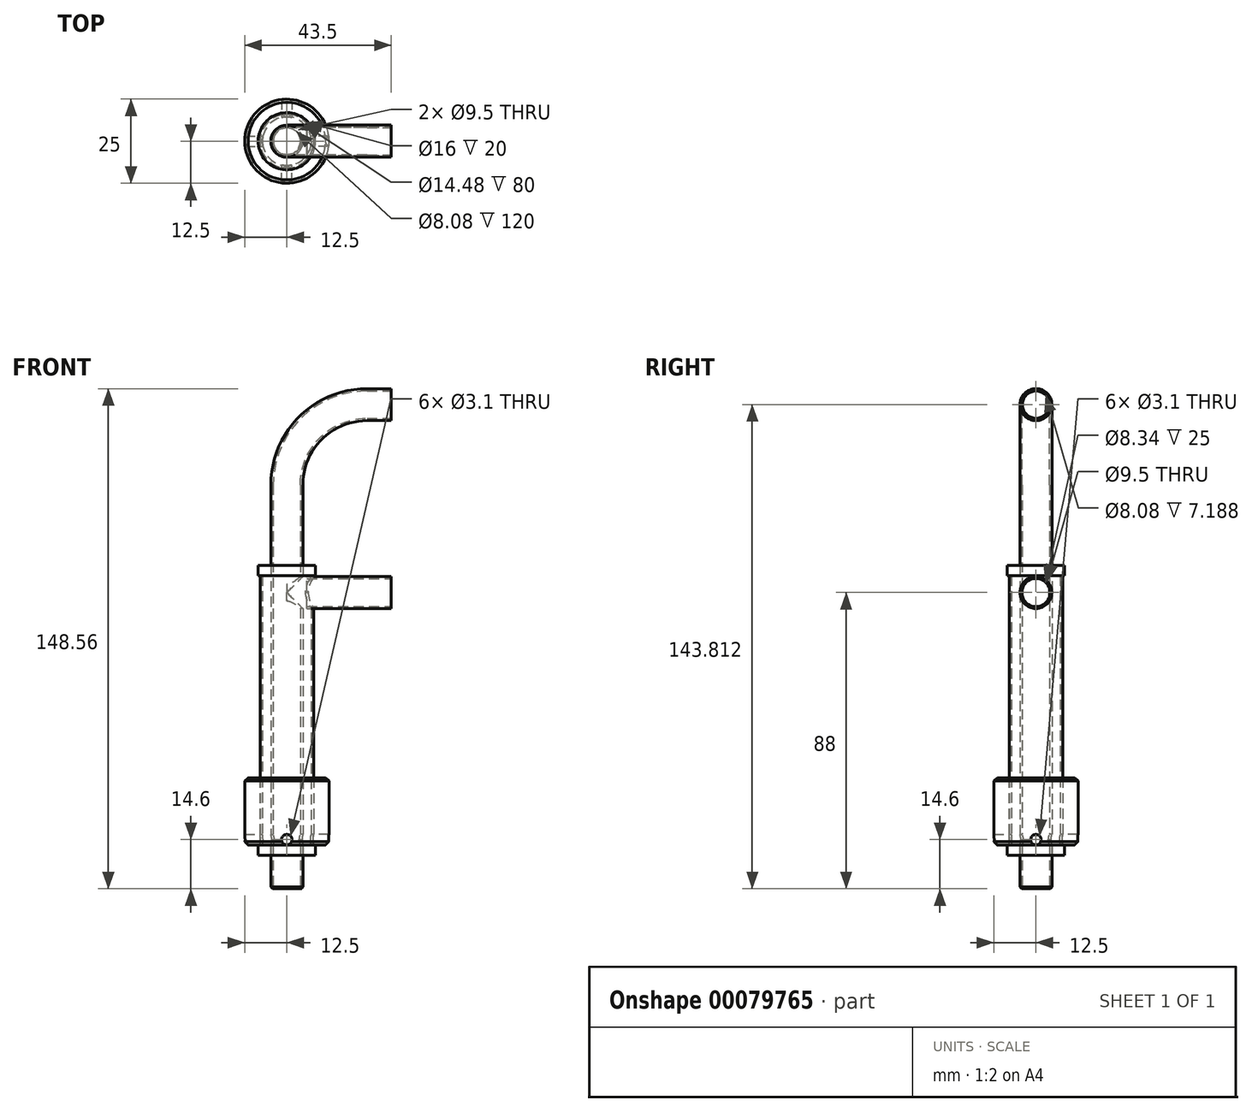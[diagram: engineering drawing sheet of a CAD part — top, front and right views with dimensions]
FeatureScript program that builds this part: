
annotation { "Feature Type Name" : "Feature", "Feature Type Description" : "" }
export const myFeature = defineFeature(function(context is Context, id is Id, definition is map)
    precondition{}
    {
        {
            var Q0;
            Q0=qCreatedBy(makeId("Top.planeOp"),FACE);
            var sketch = newSketch(context, id + "F0", { "sketchPlane" : qUnion([Q0])});
            skCircle(sketch, "E0", {"center": v(0, 0) * mm, "radius": 4.75 * mm});
            skCircle(sketch, "E1", {"center": v(0, 0) * mm, "radius": 4.04 * mm});
            skCircle(sketch, "E2", {"center": v(0, 0) * mm, "radius": 7.24 * mm});
            skCircle(sketch, "E3", {"center": v(0, 0) * mm, "radius": 7.95 * mm});
            skCircle(sketch, "E4", {"center": v(0, 0) * mm, "radius": 8.5 * mm});
            skSolve(sketch);
        }
        {
            var Q0;
            Q0=makeQuery(id+"F0.imprint","IMPRINT",FACE,{"disambiguationData":[TD([[makeQuery(id+"F0.imprint","IMPRINT",EDGE,{"derivedFrom":sQuery(id+"F0.wireOp",EDGE,"E0")}),1.0]])]});
            extrude(context, id + "F1", {"entities" : qUnion([Q0]), "depth" : 107 * mm, "hasSecondDirection" : true, "secondDirectionOppositeDirection" : true, "secondDirectionDepth" : 13 * mm});
        }
        {
            var Q0;
            Q0=makeQuery(id+"F0.imprint","IMPRINT",FACE,{"disambiguationData":[TD([[makeQuery(id+"F0.imprint","IMPRINT",EDGE,{"derivedFrom":sQuery(id+"F0.wireOp",EDGE,"E2")}),-1.0]])]});
            extrude(context, id + "F2", {"entities" : qUnion([Q0]), "depth" : 80 * mm});
        }
        {
            var Q0;
            Q0=makeQuery(id+"F0.imprint","IMPRINT",FACE,{"disambiguationData":[TD([[makeQuery(id+"F0.imprint","IMPRINT",EDGE,{"derivedFrom":sQuery(id+"F0.wireOp",EDGE,"E3")}),-1.0]])]});
            var Q1;
            Q1=makeQuery(id+"F0.imprint","IMPRINT",FACE,{"disambiguationData":[TD([[makeQuery(id+"F0.imprint","IMPRINT",EDGE,{"derivedFrom":sQuery(id+"F0.wireOp",EDGE,"E0")}),-1.0]])]});
            var Q2;
            Q2=makeQuery(id+"F0.imprint","IMPRINT",FACE,{"disambiguationData":[TD([[makeQuery(id+"F0.imprint","IMPRINT",EDGE,{"derivedFrom":sQuery(id+"F0.wireOp",EDGE,"E2")}),-1.0]])]});
            extrude(context, id + "F3", {"entities" : qUnion([Q0, Q1, Q2]), "oppositeDirection" : true, "depth" : 3 * mm});
        }
        {
            var Q0;
            Q0=qCreatedBy(makeId("Front.planeOp"),FACE);
            var sketch = newSketch(context, id + "F4", { "sketchPlane" : qUnion([Q0])});
            skLineSegment(sketch, "E5.bottom", {"start": v(8, 0) * mm, "end": v(12.5, 0) * mm});
            skLineSegment(sketch, "E5.top", {"start": v(8, 20) * mm, "end": v(12.5, 20) * mm});
            skLineSegment(sketch, "E5.left", {"start": v(8, 0) * mm, "end": v(8, 20) * mm});
            skLineSegment(sketch, "E5.right", {"start": v(12.5, 0) * mm, "end": v(12.5, 20) * mm});
            skLineSegment(sketch, "E6", {"start": v(0, 0) * mm, "end": v(0, 16.7) * mm, "construction": true});
            skSolve(sketch);
        }
        {
            var Q0;
            Q0=makeQuery(id+"F4.imprint","IMPRINT",FACE,{"disambiguationData":[TD([[makeQuery(id+"F4.imprint","IMPRINT",EDGE,{"derivedFrom":sQuery(id+"F4.wireOp",EDGE,"E5.bottom")}),1.0]])]});
            var Q1;
            Q1=sQuery(id+"F4.wireOp",EDGE,"E6");
            revolve(context, id + "F5", {"entities" : qUnion([Q0]), "axis" : qUnion([Q1]), "revolveType" : RevolveType.FULL});
        }
        {
            var Q0;
            Q0=qCreatedBy(makeId("Front.planeOp"),FACE);
            var sketch = newSketch(context, id + "F6", { "sketchPlane" : qUnion([Q0])});
            skCircle(sketch, "E7", {"center": v(0, 1.6) * mm, "radius": 1.55 * mm});
            skSolve(sketch);
        }
        {
            var Q0;
            Q0=qSketchRegion(id+"F6",true);
            extrude(context, id + "F7", {"entities" : qUnion([Q0]), "operationType" : NewBodyOperationType.REMOVE, "endBound" : BoundingType.THROUGH_ALL, "oppositeDirection" : true, "depth" : 25 * mm});
        }
        {
            var Q0;
            Q0=makeQuery(id+"F7.boolean.opBoolean","COPY",FACE,{"derivedFrom":makeQuery(id+"F7.opExtrude","SWEPT_FACE",FACE,{"disambiguationData":[OSD([sQuery(id+"F6.wireOp",EDGE,"E7")])]})});
            var Q1;
            Q1=makeQuery(id+"F2.opExtrude","SWEPT_FACE",FACE,{"disambiguationData":[OSD([sQuery(id+"F0.wireOp",EDGE,"E3")])]});
            circularPattern(context, id + "F8", {"faces" : qUnion([Q0]), "axis" : qUnion([Q1]), "angle" : 360 * degree, "instanceCount" : round(4), "equalSpace" : true, "patternType" : PatternType.FACE});
        }
        {
            var Q0;
            Q0=makeQuery(id+"F1.opExtrude","CAP_EDGE",EDGE,{"disambiguationData":[OSD([sQuery(id+"F0.wireOp",EDGE,"E0")])],"isStart":true});
            chamfer(context, id + "F9", {"entities" : qUnion([Q0]), "width" : 0.5 * mm, "tangentPropagation" : true});
        }
        {
            var Q0;
            Q0=makeQuery(id+"F2.opExtrude","CAP_FACE",FACE,{"disambiguationData":[OSD([sQuery(id+"F0.wireOp",EDGE,"E2"),sQuery(id+"F0.wireOp",EDGE,"E3")])],"isStart":false});
            var sketch = newSketch(context, id + "F10", { "sketchPlane" : qUnion([Q0])});
            skCircle(sketch, "E8", {"center": v(0, 0) * mm, "radius": 8.5 * mm});
            skCircle(sketch, "E9.0", {"center": v(0, 0) * mm, "radius": 4.75 * mm});
            skSolve(sketch);
        }
        {
            var Q0;
            Q0=qSketchRegion(id+"F10",true);
            extrude(context, id + "F11", {"entities" : qUnion([Q0]), "depth" : 3 * mm});
        }
        {
            var Q0;
            Q0=qCreatedBy(makeId("Right.planeOp"),FACE);
            var sketch = newSketch(context, id + "F12", { "sketchPlane" : qUnion([Q0])});
            skCircle(sketch, "E10", {"center": v(0, 75) * mm, "radius": 4.75 * mm});
            skSolve(sketch);
        }
        {
            var Q0;
            Q0=qSketchRegion(id+"F12",true);
            extrude(context, id + "F13", {"entities" : qUnion([Q0]), "operationType" : NewBodyOperationType.REMOVE, "endBound" : BoundingType.THROUGH_ALL, "depth" : 25 * mm});
        }
        {
            var Q0;
            Q0=qCreatedBy(makeId("Right.planeOp"),FACE);
            cPlane(context, id + "F14", {"entities" : qUnion([Q0]), "cplaneType" : CPlaneType.OFFSET, "offset" : 31 * mm, "width" : 150 * mm, "height" : 150 * mm});
        }
        {
            var Q0;
            Q0=qCreatedBy(id+"F14.planeOp",FACE);
            var sketch = newSketch(context, id + "F15", { "sketchPlane" : qUnion([Q0])});
            skCircle(sketch, "E11", {"center": v(0, 75) * mm, "radius": 4.17 * mm});
            skCircle(sketch, "E12", {"center": v(0, 75) * mm, "radius": 4.75 * mm});
            skSolve(sketch);
        }
        {
            var Q0;
            Q0=makeQuery(id+"F15.imprint","IMPRINT",FACE,{"disambiguationData":[TD([[makeQuery(id+"F15.imprint","IMPRINT",EDGE,{"derivedFrom":sQuery(id+"F15.wireOp",EDGE,"E11")}),-1.0]])]});
            var Q1;
            Q1=makeQuery(id+"F2.opExtrude","SWEPT_FACE",FACE,{"disambiguationData":[OSD([sQuery(id+"F0.wireOp",EDGE,"E2")])]});
            extrude(context, id + "F16", {"entities" : qUnion([Q0]), "oppositeDirection" : true, "endBoundEntityFace" : qUnion([Q1]), "depth" : 25 * mm});
        }
        {
            var Q0;
            Q0=qCreatedBy(makeId("Front.planeOp"),FACE);
            var sketch = newSketch(context, id + "F17", { "sketchPlane" : qUnion([Q0])});
            skPoint(sketch, "E13.0", {"position": v(31, 75) * mm});
            skArc(sketch, "E14", {"start": v(31, 75) * mm, "mid": v(41.08, 79.17) * mm, "end": v(45.25, 89.25) * mm});
            skLineSegment(sketch, "E15", {"start": v(45.25, 89.25) * mm, "end": v(45.25, 119.25) * mm});
            skSolve(sketch);
        }
        {
            var Q0;
            Q0=makeQuery(id+"F5.opRevolve","SWEPT_EDGE",EDGE,{"disambiguationData":[OSD([sQuery(id+"F4.wireOp",EDGE,"E5.bottom"),sQuery(id+"F4.wireOp",EDGE,"E5.right")])]});
            var Q1;
            Q1=makeQuery(id+"F5.opRevolve","SWEPT_EDGE",EDGE,{"disambiguationData":[OSD([sQuery(id+"F4.wireOp",EDGE,"E5.top"),sQuery(id+"F4.wireOp",EDGE,"E5.right")])]});
            chamfer(context, id + "F18", {"entities" : qUnion([Q0, Q1]), "width" : 1 * mm, "tangentPropagation" : true});
        }
        {
            var Q0;
            Q0=qCreatedBy(makeId("Front.planeOp"),FACE);
            var sketch = newSketch(context, id + "F19", { "sketchPlane" : qUnion([Q0])});
            skLineSegment(sketch, "E16.0", {"start": v(-4.04, 107) * mm, "end": v(4.04, 107) * mm, "construction": true});
            skLineSegment(sketch, "E17", {"start": v(23.81, 130.81) * mm, "end": v(31, 130.81) * mm});
            skArc(sketch, "E18", {"start": v(23.81, 130.81) * mm, "mid": v(6.97, 123.84) * mm, "end": v(0, 107) * mm});
            skLineSegment(sketch, "E19", {"start": v(0, 107) * mm, "end": v(0, 104) * mm, "construction": true});
            skSolve(sketch);
        }
        {
            var Q0;
            Q0=makeQuery(id+"F1.opExtrude","CAP_FACE",FACE,{"disambiguationData":[OSD([sQuery(id+"F0.wireOp",EDGE,"E0"),sQuery(id+"F0.wireOp",EDGE,"E1")])],"isStart":false});
            var Q1;
            Q1=sQuery(id+"F19.wireOp",EDGE,"E18");
            var Q2;
            Q2=sQuery(id+"F19.wireOp",EDGE,"E17");
            sweep(context, id + "F20", {"operationType" : NewBodyOperationType.ADD, "profiles" : qUnion([Q0]), "path" : qUnion([Q1, Q2])});
        }
    });
